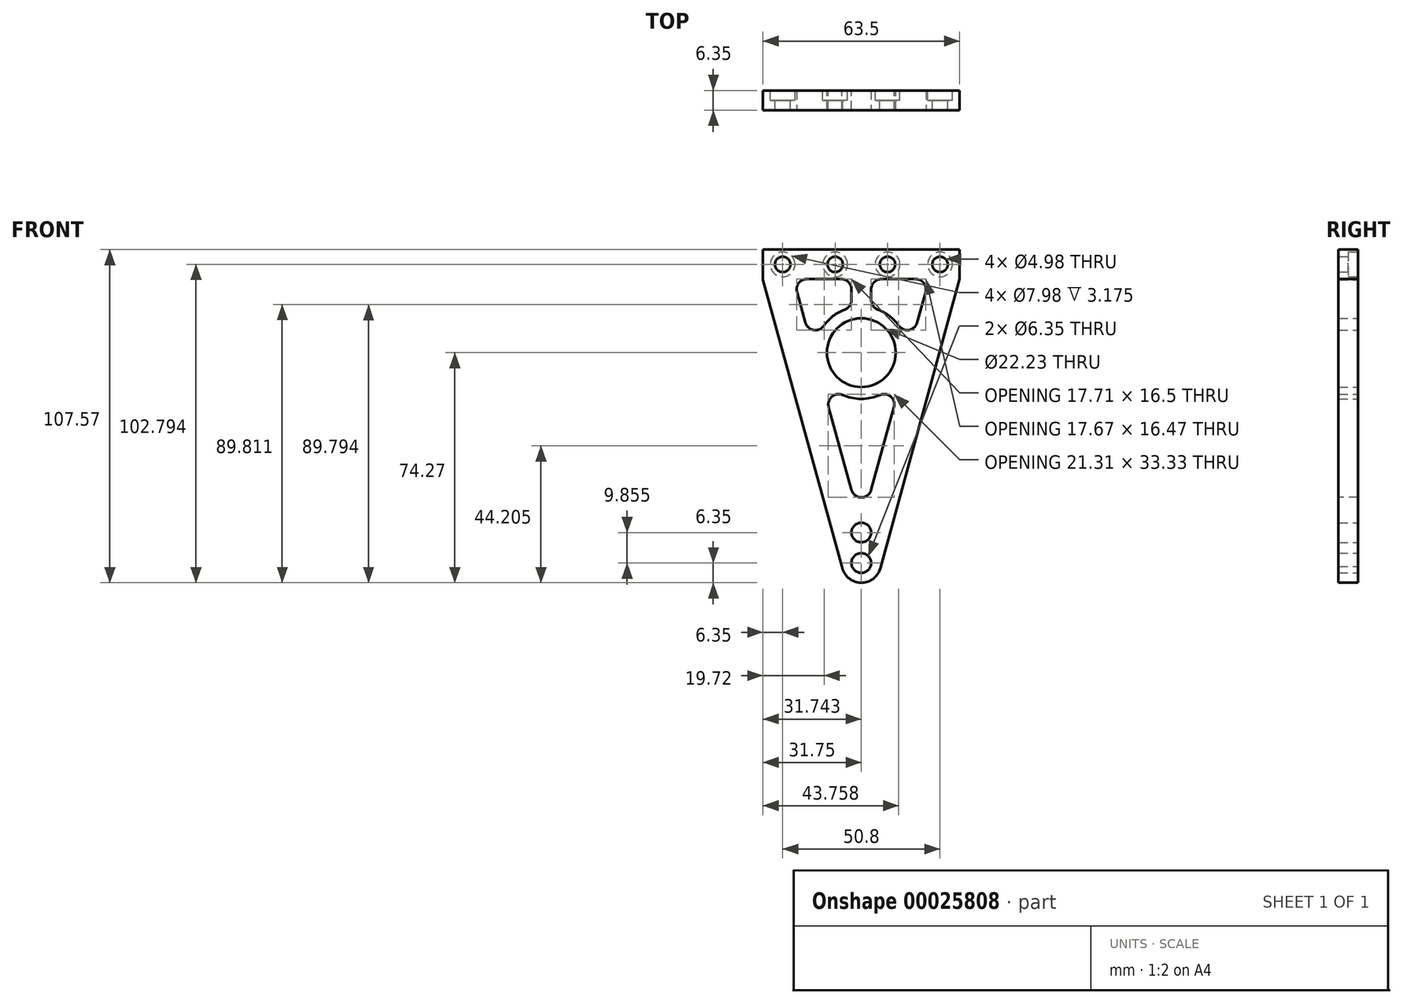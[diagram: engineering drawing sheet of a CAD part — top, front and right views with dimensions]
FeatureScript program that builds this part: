
annotation { "Feature Type Name" : "Feature", "Feature Type Description" : "" }
export const myFeature = defineFeature(function(context is Context, id is Id, definition is map)
    precondition{}
    {
        {
            var Q0;
            Q0=qCreatedBy(makeId("Front.planeOp"),FACE);
            var sketch = newSketch(context, id + "F0", { "sketchPlane" : qUnion([Q0])});
            skCircle(sketch, "E0", {"center": v(0, 0) * mm, "radius": 11.11 * mm});
            skLineSegment(sketch, "E1", {"start": v(0, 0) * mm, "end": v(0, 55.13) * mm, "construction": true});
            skLineSegment(sketch, "E2", {"start": v(0, 0) * mm, "end": v(42.92, 0) * mm, "construction": true});
            skLineSegment(sketch, "E3", {"start": v(31.75, 33.3) * mm, "end": v(31.75, 23.77) * mm});
            skLineSegment(sketch, "E4", {"start": v(-31.75, 23.6) * mm, "end": v(-31.75, 33.3) * mm});
            skLineSegment(sketch, "E5", {"start": v(-31.75, 33.3) * mm, "end": v(31.75, 33.3) * mm});
            skLineSegment(sketch, "E6", {"start": v(31.75, 23.77) * mm, "end": v(6.12, -69.6) * mm});
            skLineSegment(sketch, "E7", {"start": v(-6.25, -69.03) * mm, "end": v(-31.75, 23.6) * mm});
            skPoint(sketch, "E8.orphan", {"position": v(31.75, 14.25) * mm});
            skArc(sketch, "E9", {"start": v(-6.25, -69.03) * mm, "mid": v(-0.3, -74.26) * mm, "end": v(6.12, -69.6) * mm});
            skPoint(sketch, "E10.start.orphan", {"position": v(15.69, -34.74) * mm});
            skPoint(sketch, "E11.orphan", {"position": v(-15.69, -34.74) * mm});
            skLineSegment(sketch, "E12", {"start": v(28.8, 28.52) * mm, "end": v(-20.75, 28.52) * mm, "construction": true});
            skCircle(sketch, "E13", {"center": v(25.4, 28.52) * mm, "radius": 3.99 * mm});
            skCircle(sketch, "E14", {"center": v(8.46, 28.52) * mm, "radius": 3.99 * mm});
            skCircle(sketch, "E15", {"center": v(-8.46, 28.52) * mm, "radius": 3.99 * mm});
            skCircle(sketch, "E16", {"center": v(-25.4, 28.52) * mm, "radius": 3.99 * mm});
            skCircle(sketch, "E17", {"center": v(25.4, 28.52) * mm, "radius": 2.49 * mm});
            skCircle(sketch, "E18", {"center": v(8.46, 28.52) * mm, "radius": 2.49 * mm});
            skCircle(sketch, "E19", {"center": v(-8.46, 28.52) * mm, "radius": 2.49 * mm});
            skCircle(sketch, "E20", {"center": v(-25.4, 28.52) * mm, "radius": 2.49 * mm});
            skSolve(sketch);
        }
        {
            var Q0;
            Q0=makeQuery(id+"F0.imprint","IMPRINT",FACE,{"disambiguationData":[TD([[makeQuery(id+"F0.imprint","IMPRINT",EDGE,{"derivedFrom":sQuery(id+"F0.wireOp",EDGE,"E0")}),-1.0]])]});
            var Q1;
            Q1=makeQuery(id+"F0.imprint","IMPRINT",FACE,{"disambiguationData":[TD([[makeQuery(id+"F0.imprint","IMPRINT",EDGE,{"derivedFrom":sQuery(id+"F0.wireOp",EDGE,"E13")}),1.0]])]});
            var Q2;
            Q2=makeQuery(id+"F0.imprint","IMPRINT",FACE,{"disambiguationData":[TD([[makeQuery(id+"F0.imprint","IMPRINT",EDGE,{"derivedFrom":sQuery(id+"F0.wireOp",EDGE,"E14")}),1.0]])]});
            var Q3;
            Q3=makeQuery(id+"F0.imprint","IMPRINT",FACE,{"disambiguationData":[TD([[makeQuery(id+"F0.imprint","IMPRINT",EDGE,{"derivedFrom":sQuery(id+"F0.wireOp",EDGE,"E15")}),1.0]])]});
            var Q4;
            Q4=makeQuery(id+"F0.imprint","IMPRINT",FACE,{"disambiguationData":[TD([[makeQuery(id+"F0.imprint","IMPRINT",EDGE,{"derivedFrom":sQuery(id+"F0.wireOp",EDGE,"E16")}),1.0]])]});
            extrude(context, id + "F1", {"entities" : qUnion([Q0, Q1, Q2, Q3, Q4]), "depth" : 6.35 * mm});
        }
        {
            var Q0;
            Q0=makeQuery(id+"F1.opExtrude","CAP_FACE",FACE,{"disambiguationData":[OSD([sQuery(id+"F0.wireOp",EDGE,"E0"),sQuery(id+"F0.wireOp",EDGE,"E3"),sQuery(id+"F0.wireOp",EDGE,"E4"),sQuery(id+"F0.wireOp",EDGE,"E5"),sQuery(id+"F0.wireOp",EDGE,"E6"),sQuery(id+"F0.wireOp",EDGE,"E7"),sQuery(id+"F0.wireOp",EDGE,"E9"),sQuery(id+"F0.wireOp",EDGE,"E17"),sQuery(id+"F0.wireOp",EDGE,"E18"),sQuery(id+"F0.wireOp",EDGE,"E19"),sQuery(id+"F0.wireOp",EDGE,"E20")])],"isStart":true});
            var sketch = newSketch(context, id + "F2", { "sketchPlane" : qUnion([Q0])});
            skLineSegment(sketch, "E21.1", {"start": v(21.92, 23.77) * mm, "end": v(-21.87, 23.77) * mm});
            skLineSegment(sketch, "E21.3", {"start": v(0, -55.89) * mm, "end": v(13.84, -5.6) * mm});
            skLineSegment(sketch, "E21.5", {"start": v(-21.87, 23.77) * mm, "end": v(-14.78, -2.08) * mm});
            skArc(sketch, "E22", {"start": v(-13.77, -5.75) * mm, "mid": v(0.09, -14.92) * mm, "end": v(13.84, -5.6) * mm});
            skLineSegment(sketch, "E23.trimOffspring", {"start": v(-13.77, -5.75) * mm, "end": v(0, -55.89) * mm});
            skLineSegment(sketch, "E24.trimOffspring", {"start": v(14.75, -2.28) * mm, "end": v(21.92, 23.77) * mm});
            skArc(sketch, "E25.trimOffspring", {"start": v(14.75, -2.28) * mm, "mid": v(0.1, 14.92) * mm, "end": v(-14.78, -2.08) * mm});
            skLineSegment(sketch, "E26", {"start": v(0, 59.66) * mm, "end": v(0, -55.85) * mm});
            skLineSegment(sketch, "E27", {"start": v(-3.17, 23.77) * mm, "end": v(-3.17, 14.58) * mm});
            skLineSegment(sketch, "E28", {"start": v(3.18, 23.77) * mm, "end": v(3.18, 14.58) * mm});
            skSolve(sketch);
        }
        {
            var Q0;
            {var subQ2=sQuery(id+"F2.wireOp",EDGE,"E21.5");Q0=makeQuery(id+"F2.imprint","IMPRINT",FACE,{"disambiguationData":[TD([[makeQuery(id+"F2.imprint","IMPRINT",EDGE,{"derivedFrom":subQ2}),1.0]])]});}
            var Q1;
            {var subQ2=sQuery(id+"F2.wireOp",EDGE,"E24.trimOffspring");Q1=makeQuery(id+"F2.imprint","IMPRINT",FACE,{"disambiguationData":[TD([[makeQuery(id+"F2.imprint","IMPRINT",EDGE,{"derivedFrom":subQ2}),1.0]])]});}
            var Q2;
            {var subQ5=sQuery(id+"F2.wireOp",EDGE,"E23.trimOffspring");Q2=makeQuery(id+"F2.imprint","IMPRINT",FACE,{"disambiguationData":[TD([[makeQuery(id+"F2.imprint","IMPRINT",EDGE,{"derivedFrom":subQ5}),1.0]])]});}
            var Q3;
            {var subQ1=sQuery(id+"F2.wireOp",EDGE,"E22");var subQ3=sQuery(id+"F2.wireOp",EDGE,"E21.3");var subQ5=makeQuery(id+"F2.imprint","INTERSECT",VERTEX,{"derivedFrom":[subQ3,subQ1]});Q3=makeQuery(id+"F2.imprint","IMPRINT",FACE,{"disambiguationData":[TD([[makeQuery(id+"F2.imprint","IMPRINT",EDGE,{"disambiguationData":[TD([[subQ5,1.0]])],"derivedFrom":subQ3}),1.0]])]});}
            extrude(context, id + "F3", {"entities" : qUnion([Q0, Q1, Q2, Q3]), "operationType" : NewBodyOperationType.REMOVE, "endBound" : BoundingType.THROUGH_ALL, "oppositeDirection" : true, "depth" : 25.4 * mm});
        }
        {
            var Q0;
            Q0=makeQuery(id+"F3.boolean.opBoolean","COPY",EDGE,{"derivedFrom":makeQuery(id+"F3.opExtrude","SWEPT_EDGE",EDGE,{"disambiguationData":[OSD([sQuery(id+"F2.wireOp",EDGE,"E21.3"),sQuery(id+"F2.wireOp",EDGE,"E23.trimOffspring")])]})});
            var Q1;
            Q1=makeQuery(id+"F3.boolean.opBoolean","COPY",EDGE,{"derivedFrom":makeQuery(id+"F3.opExtrude","SWEPT_EDGE",EDGE,{"disambiguationData":[OSD([sQuery(id+"F2.wireOp",EDGE,"E21.1"),sQuery(id+"F2.wireOp",EDGE,"E21.5")])]})});
            var Q2;
            Q2=makeQuery(id+"F3.boolean.opBoolean","COPY",EDGE,{"derivedFrom":makeQuery(id+"F3.opExtrude","SWEPT_EDGE",EDGE,{"disambiguationData":[OSD([sQuery(id+"F2.wireOp",EDGE,"E21.1"),sQuery(id+"F2.wireOp",EDGE,"E28")])]})});
            var Q3;
            Q3=makeQuery(id+"F3.boolean.opBoolean","COPY",EDGE,{"derivedFrom":makeQuery(id+"F3.opExtrude","SWEPT_EDGE",EDGE,{"disambiguationData":[OSD([sQuery(id+"F2.wireOp",EDGE,"E25.trimOffspring"),sQuery(id+"F2.wireOp",EDGE,"E28")])]})});
            var Q4;
            Q4=makeQuery(id+"F3.boolean.opBoolean","COPY",EDGE,{"derivedFrom":makeQuery(id+"F3.opExtrude","SWEPT_EDGE",EDGE,{"disambiguationData":[OSD([sQuery(id+"F2.wireOp",EDGE,"E21.1"),sQuery(id+"F2.wireOp",EDGE,"E24.trimOffspring")])]})});
            var Q5;
            Q5=makeQuery(id+"F3.boolean.opBoolean","COPY",EDGE,{"derivedFrom":makeQuery(id+"F3.opExtrude","SWEPT_EDGE",EDGE,{"disambiguationData":[OSD([sQuery(id+"F2.wireOp",EDGE,"E21.1"),sQuery(id+"F2.wireOp",EDGE,"E27")])]})});
            var Q6;
            Q6=makeQuery(id+"F3.boolean.opBoolean","COPY",EDGE,{"derivedFrom":makeQuery(id+"F3.opExtrude","SWEPT_EDGE",EDGE,{"disambiguationData":[OSD([sQuery(id+"F2.wireOp",EDGE,"E24.trimOffspring"),sQuery(id+"F2.wireOp",EDGE,"E25.trimOffspring")])]})});
            var Q7;
            Q7=makeQuery(id+"F3.boolean.opBoolean","COPY",EDGE,{"derivedFrom":makeQuery(id+"F3.opExtrude","SWEPT_EDGE",EDGE,{"disambiguationData":[OSD([sQuery(id+"F2.wireOp",EDGE,"E21.5"),sQuery(id+"F2.wireOp",EDGE,"E25.trimOffspring")])]})});
            var Q8;
            Q8=makeQuery(id+"F3.boolean.opBoolean","COPY",EDGE,{"derivedFrom":makeQuery(id+"F3.opExtrude","SWEPT_EDGE",EDGE,{"disambiguationData":[OSD([sQuery(id+"F2.wireOp",EDGE,"E22"),sQuery(id+"F2.wireOp",EDGE,"E23.trimOffspring")])]})});
            var Q9;
            Q9=makeQuery(id+"F3.boolean.opBoolean","COPY",EDGE,{"derivedFrom":makeQuery(id+"F3.opExtrude","SWEPT_EDGE",EDGE,{"disambiguationData":[OSD([sQuery(id+"F2.wireOp",EDGE,"E21.3"),sQuery(id+"F2.wireOp",EDGE,"E22")])]})});
            var Q10;
            Q10=makeQuery(id+"F3.boolean.opBoolean","COPY",EDGE,{"derivedFrom":makeQuery(id+"F3.opExtrude","SWEPT_EDGE",EDGE,{"disambiguationData":[OSD([sQuery(id+"F2.wireOp",EDGE,"E25.trimOffspring"),sQuery(id+"F2.wireOp",EDGE,"E27")])]})});
            fillet(context, id + "F4", {"entities" : qUnion([Q0, Q1, Q2, Q3, Q4, Q5, Q6, Q7, Q8, Q9, Q10]), "radius" : 3.3 * mm, "tangentPropagation" : true, "allowEdgeOverflow" : false});
        }
        {
            var Q0;
            Q0=makeQuery(id+"F1.opExtrude","CAP_FACE",FACE,{"disambiguationData":[OSD([sQuery(id+"F0.wireOp",EDGE,"E0"),sQuery(id+"F0.wireOp",EDGE,"E3"),sQuery(id+"F0.wireOp",EDGE,"E4"),sQuery(id+"F0.wireOp",EDGE,"E5"),sQuery(id+"F0.wireOp",EDGE,"E6"),sQuery(id+"F0.wireOp",EDGE,"E7"),sQuery(id+"F0.wireOp",EDGE,"E9"),sQuery(id+"F0.wireOp",EDGE,"E17"),sQuery(id+"F0.wireOp",EDGE,"E18"),sQuery(id+"F0.wireOp",EDGE,"E19"),sQuery(id+"F0.wireOp",EDGE,"E20")])],"isStart":true});
            var sketch = newSketch(context, id + "F5", { "sketchPlane" : qUnion([Q0])});
            skCircle(sketch, "E29", {"center": v(-25.4, 28.52) * mm, "radius": 3.99 * mm});
            skCircle(sketch, "E30", {"center": v(-8.46, 28.52) * mm, "radius": 3.99 * mm});
            skCircle(sketch, "E31", {"center": v(8.46, 28.52) * mm, "radius": 3.99 * mm});
            skCircle(sketch, "E32", {"center": v(25.4, 28.52) * mm, "radius": 3.99 * mm});
            skCircle(sketch, "E33", {"center": v(-25.4, 28.52) * mm, "radius": 2.49 * mm});
            skCircle(sketch, "E34", {"center": v(-8.46, 28.52) * mm, "radius": 2.49 * mm});
            skCircle(sketch, "E35", {"center": v(8.46, 28.52) * mm, "radius": 2.49 * mm});
            skCircle(sketch, "E36", {"center": v(25.4, 28.52) * mm, "radius": 2.49 * mm});
            skSolve(sketch);
        }
        {
            var Q0;
            Q0=makeQuery(id+"F5.imprint","IMPRINT",FACE,{"disambiguationData":[TD([[makeQuery(id+"F5.imprint","IMPRINT",EDGE,{"derivedFrom":sQuery(id+"F5.wireOp",EDGE,"E29")}),1.0]])]});
            var Q1;
            Q1=makeQuery(id+"F5.imprint","IMPRINT",FACE,{"disambiguationData":[TD([[makeQuery(id+"F5.imprint","IMPRINT",EDGE,{"derivedFrom":sQuery(id+"F5.wireOp",EDGE,"E30")}),1.0]])]});
            var Q2;
            Q2=makeQuery(id+"F5.imprint","IMPRINT",FACE,{"disambiguationData":[TD([[makeQuery(id+"F5.imprint","IMPRINT",EDGE,{"derivedFrom":sQuery(id+"F5.wireOp",EDGE,"E31")}),1.0]])]});
            var Q3;
            Q3=makeQuery(id+"F5.imprint","IMPRINT",FACE,{"disambiguationData":[TD([[makeQuery(id+"F5.imprint","IMPRINT",EDGE,{"derivedFrom":sQuery(id+"F5.wireOp",EDGE,"E32")}),1.0]])]});
            extrude(context, id + "F6", {"entities" : qUnion([Q0, Q1, Q2, Q3]), "operationType" : NewBodyOperationType.REMOVE, "oppositeDirection" : true, "depth" : 3.17 * mm});
        }
        {
            var Q0;
            Q0=makeQuery(id+"F1.opExtrude","CAP_FACE",FACE,{"disambiguationData":[OSD([sQuery(id+"F0.wireOp",EDGE,"E0"),sQuery(id+"F0.wireOp",EDGE,"E3"),sQuery(id+"F0.wireOp",EDGE,"E4"),sQuery(id+"F0.wireOp",EDGE,"E5"),sQuery(id+"F0.wireOp",EDGE,"E6"),sQuery(id+"F0.wireOp",EDGE,"E7"),sQuery(id+"F0.wireOp",EDGE,"E9"),sQuery(id+"F0.wireOp",EDGE,"E17"),sQuery(id+"F0.wireOp",EDGE,"E18"),sQuery(id+"F0.wireOp",EDGE,"E19"),sQuery(id+"F0.wireOp",EDGE,"E20")])],"isStart":true});
            var sketch = newSketch(context, id + "F7", { "sketchPlane" : qUnion([Q0])});
            skCircle(sketch, "E37", {"center": v(0, -58.06) * mm, "radius": 3.17 * mm});
            skCircle(sketch, "E38", {"center": v(0, -67.92) * mm, "radius": 3.18 * mm});
            skSolve(sketch);
        }
        {
            var Q0;
            Q0=makeQuery(id+"F7.imprint","IMPRINT",FACE,{"disambiguationData":[TD([[makeQuery(id+"F7.imprint","IMPRINT",EDGE,{"derivedFrom":sQuery(id+"F7.wireOp",EDGE,"E37")}),1.0]])]});
            var Q1;
            Q1=makeQuery(id+"F7.imprint","IMPRINT",FACE,{"disambiguationData":[TD([[makeQuery(id+"F7.imprint","IMPRINT",EDGE,{"derivedFrom":sQuery(id+"F7.wireOp",EDGE,"E38")}),1.0]])]});
            extrude(context, id + "F8", {"entities" : qUnion([Q0, Q1]), "operationType" : NewBodyOperationType.REMOVE, "endBound" : BoundingType.THROUGH_ALL, "oppositeDirection" : true, "depth" : 25.4 * mm});
        }
    });
